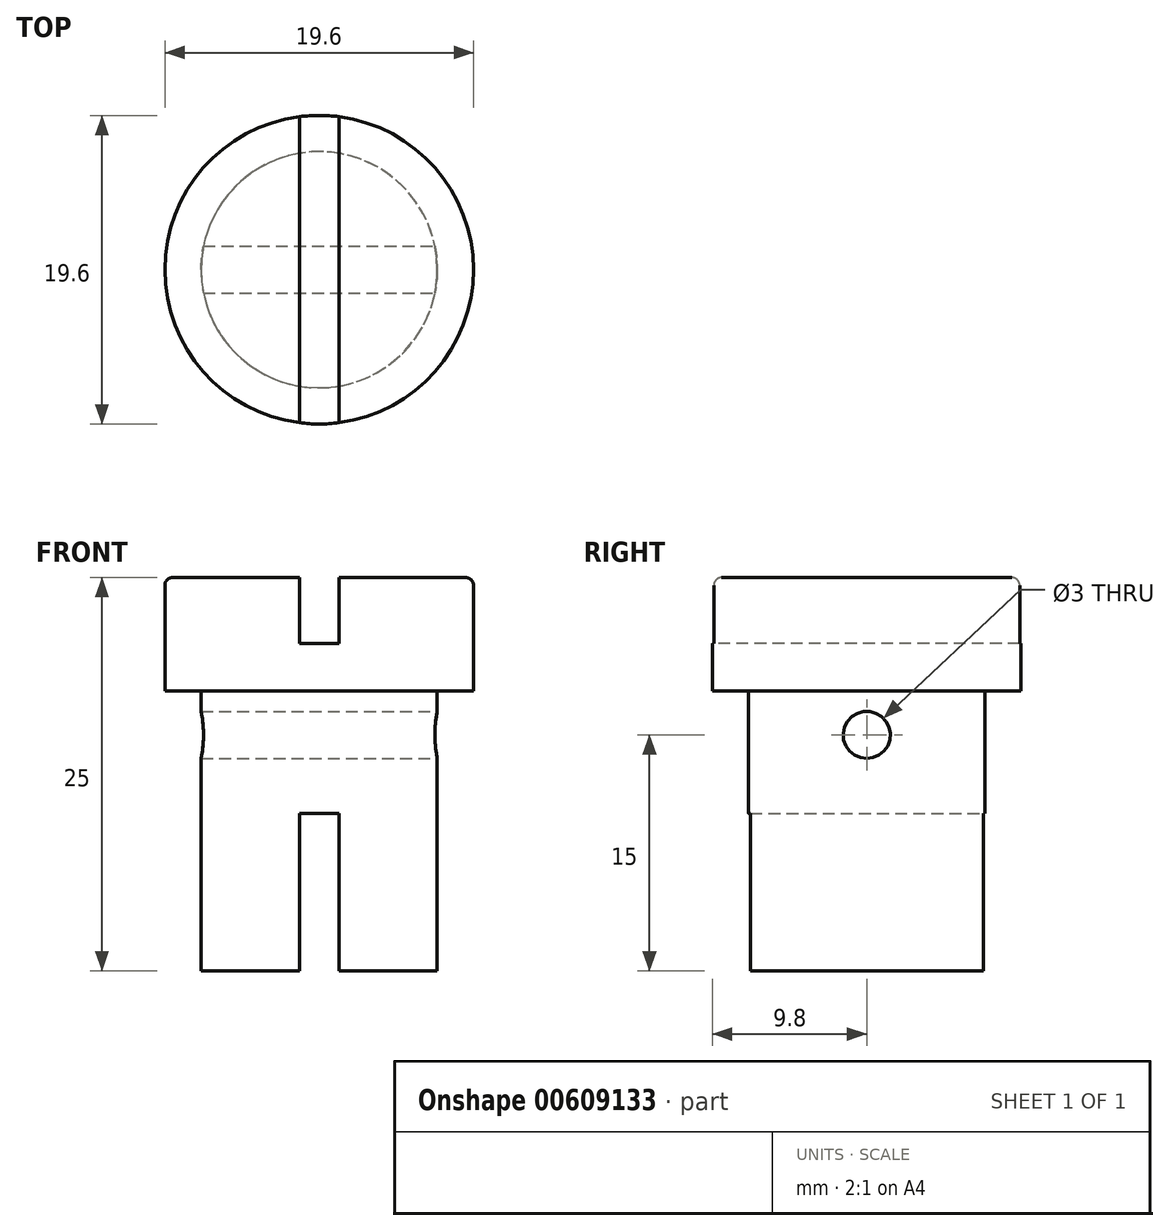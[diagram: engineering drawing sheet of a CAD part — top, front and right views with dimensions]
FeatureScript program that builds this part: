
annotation { "Feature Type Name" : "Feature", "Feature Type Description" : "" }
export const myFeature = defineFeature(function(context is Context, id is Id, definition is map)
    precondition{}
    {
        {
            var Q0;
            Q0=qCreatedBy(makeId("Front.planeOp"),FACE);
            var sketch = newSketch(context, id + "F0", { "sketchPlane" : qUnion([Q0])});
            skLineSegment(sketch, "E0", {"start": v(0, 25) * mm, "end": v(9.8, 25) * mm});
            skLineSegment(sketch, "E1", {"start": v(9.8, 25) * mm, "end": v(9.8, 17.8) * mm});
            skLineSegment(sketch, "E2", {"start": v(9.8, 17.8) * mm, "end": v(7.5, 17.8) * mm});
            skLineSegment(sketch, "E3", {"start": v(7.5, 17.8) * mm, "end": v(7.5, 0) * mm});
            skLineSegment(sketch, "E4", {"start": v(7.5, 0) * mm, "end": v(0, 0) * mm});
            skLineSegment(sketch, "E5", {"start": v(0, 0) * mm, "end": v(0, 25) * mm});
            skSolve(sketch);
        }
        {
            var Q0;
            Q0=makeQuery(id+"F0.imprint","IMPRINT",FACE,{"disambiguationData":[TD([[makeQuery(id+"F0.imprint","IMPRINT",EDGE,{"derivedFrom":sQuery(id+"F0.wireOp",EDGE,"E0")}),-1.0]])]});
            var Q1;
            Q1=sQuery(id+"F0.wireOp",EDGE,"E5");
            revolve(context, id + "F1", {"entities" : qUnion([Q0]), "axis" : qUnion([Q1]), "revolveType" : RevolveType.FULL});
        }
        {
            var Q0;
            Q0=makeQuery(id+"F1.opRevolve","SWEPT_FACE",FACE,{"disambiguationData":[OSD([sQuery(id+"F0.wireOp",EDGE,"E0")])]});
            var sketch = newSketch(context, id + "F2", { "sketchPlane" : qUnion([Q0])});
            skLineSegment(sketch, "E6", {"start": v(-1.25, 12.27) * mm, "end": v(-1.25, -12.05) * mm});
            skLineSegment(sketch, "E7.MirrorCS", {"start": v(1.25, 12.27) * mm, "end": v(1.25, -12.05) * mm});
            skLineSegment(sketch, "E8", {"start": v(-1.25, 12.27) * mm, "end": v(1.25, 12.27) * mm});
            skLineSegment(sketch, "E9", {"start": v(-1.25, -12.05) * mm, "end": v(1.25, -12.05) * mm});
            skSolve(sketch);
        }
        {
            var Q0;
            Q0 = qSketchRegion(id + "F2", true);
            extrude(context, id + "F3", {"entities" : qUnion([Q0]), "operationType" : NewBodyOperationType.REMOVE, "oppositeDirection" : true, "depth" : 4.2 * mm, "offsetDistance" : 25 * mm});
        }
        {
            var Q0;
            {var subQ0=sQuery(id+"F0.wireOp",EDGE,"E0");var subQ1=sQuery(id+"F0.wireOp",EDGE,"E1");Q0=makeQuery(id+"F3.boolean.opBoolean","SPLIT",EDGE,{"disambiguationData":[TD([makeQuery(id+"F3.opExtrude","SWEPT_FACE",FACE,{"disambiguationData":[OSD([sQuery(id+"F2.wireOp",EDGE,"E6")])]})])],"derivedFrom":makeQuery(id+"F1.opRevolve","SWEPT_EDGE",EDGE,{"disambiguationData":[OSD([subQ0,subQ1])]})});}
            var Q1;
            {var subQ0=sQuery(id+"F0.wireOp",EDGE,"E0");var subQ1=sQuery(id+"F0.wireOp",EDGE,"E1");Q1=makeQuery(id+"F3.boolean.opBoolean","SPLIT",EDGE,{"disambiguationData":[TD([makeQuery(id+"F3.opExtrude","SWEPT_FACE",FACE,{"disambiguationData":[OSD([sQuery(id+"F2.wireOp",EDGE,"E7.MirrorCS")])]})])],"derivedFrom":makeQuery(id+"F1.opRevolve","SWEPT_EDGE",EDGE,{"disambiguationData":[OSD([subQ0,subQ1])]})});}
            fillet(context, id + "F4", {"entities" : qUnion([Q0, Q1]), "radius" : .5 * mm, "tangentPropagation" : true, "allowEdgeOverflow" : false});
        }
        {
            var Q0;
            Q0=makeQuery(id+"F1.opRevolve","SWEPT_FACE",FACE,{"disambiguationData":[OSD([sQuery(id+"F0.wireOp",EDGE,"E4")])]});
            var sketch = newSketch(context, id + "F5", { "sketchPlane" : qUnion([Q0])});
            skLineSegment(sketch, "E10", {"start": v(-1.25, 12) * mm, "end": v(-1.25, -12.31) * mm});
            skLineSegment(sketch, "E11.MirrorCS", {"start": v(1.25, 12) * mm, "end": v(1.25, -12.31) * mm});
            skLineSegment(sketch, "E12", {"start": v(-1.25, -12.31) * mm, "end": v(1.25, -12.31) * mm});
            skLineSegment(sketch, "E13", {"start": v(-1.25, 12) * mm, "end": v(1.25, 12) * mm});
            skSolve(sketch);
        }
        {
            var Q0;
            {var subQ0=sQuery(id+"F5.wireOp",EDGE,"E13");Q0=makeQuery(id+"F5.imprint","IMPRINT",FACE,{"disambiguationData":[TD([[makeQuery(id+"F5.imprint","IMPRINT",EDGE,{"derivedFrom":subQ0}),-1.0]])]});}
            var Q1;
            {var subQ0=sQuery(id+"F5.wireOp",EDGE,"E12");Q1=makeQuery(id+"F5.imprint","IMPRINT",FACE,{"disambiguationData":[TD([[makeQuery(id+"F5.imprint","IMPRINT",EDGE,{"derivedFrom":subQ0}),1.0]])]});}
            var Q2;
            {var subQ0=sQuery(id+"F5.wireOp",EDGE,"E10");var subQ1=makeQuery(id+"F1.opRevolve","SWEPT_EDGE",EDGE,{"disambiguationData":[OSD([sQuery(id+"F0.wireOp",EDGE,"E3"),sQuery(id+"F0.wireOp",EDGE,"E4")])]});var subQ2=makeQuery(id+"F5.imprint","INTERSECT",VERTEX,{"disambiguationData":[OD(0.0)],"derivedFrom":[subQ1,subQ0]});Q2=makeQuery(id+"F5.imprint","IMPRINT",FACE,{"disambiguationData":[TD([[makeQuery(id+"F5.imprint","IMPRINT",EDGE,{"disambiguationData":[TD([[subQ2,-1.0]])],"derivedFrom":subQ0}),1.0]])]});}
            extrude(context, id + "F6", {"entities" : qUnion([Q0, Q1, Q2]), "operationType" : NewBodyOperationType.REMOVE, "oppositeDirection" : true, "depth" : 10 * mm, "offsetDistance" : 25 * mm});
        }
        {
            var Q0;
            Q0=qCreatedBy(makeId("Right.planeOp"),FACE);
            var sketch = newSketch(context, id + "F7", { "sketchPlane" : qUnion([Q0])});
            skCircle(sketch, "E14", {"center": v(0, 15) * mm, "radius": 1.5 * mm});
            skSolve(sketch);
        }
        {
            var Q0;
            Q0 = qSketchRegion(id + "F7", true);
            extrude(context, id + "F8", {"entities" : qUnion([Q0]), "operationType" : NewBodyOperationType.REMOVE, "endBound" : BoundingType.SYMMETRIC, "oppositeDirection" : true, "depth" : 35.6 * mm, "offsetDistance" : 25 * mm});
        }
    });
